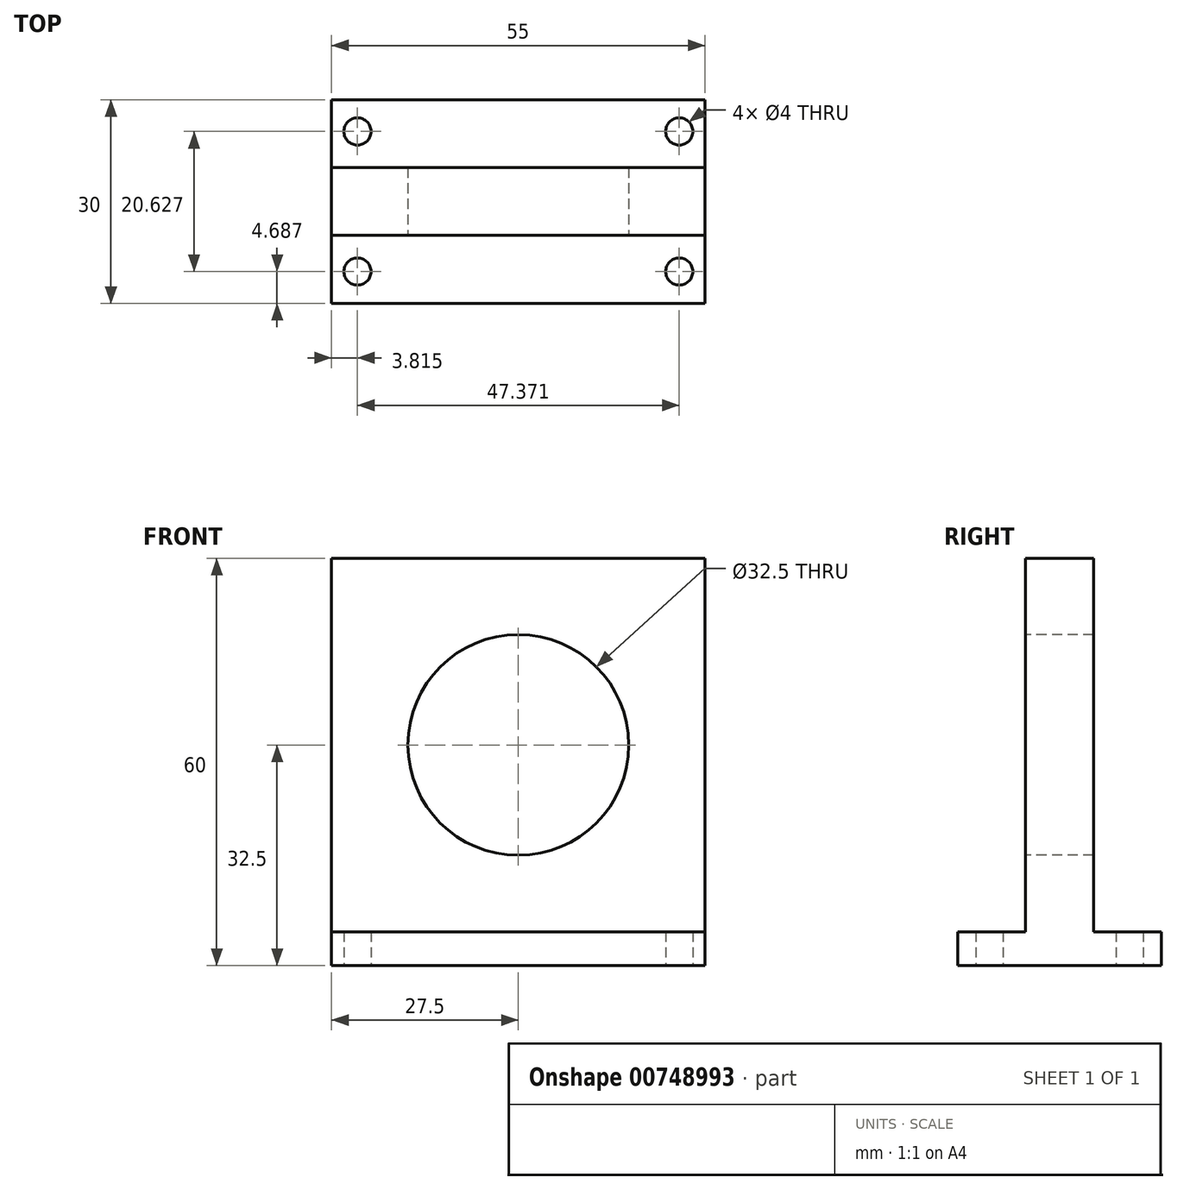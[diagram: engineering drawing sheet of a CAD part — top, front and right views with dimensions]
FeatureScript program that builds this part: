
annotation { "Feature Type Name" : "Feature", "Feature Type Description" : "" }
export const myFeature = defineFeature(function(context is Context, id is Id, definition is map)
    precondition{}
    {
        {
            var Q0;
            Q0=qCreatedBy(makeId("Top.planeOp"),FACE);
            var sketch = newSketch(context, id + "F0", { "sketchPlane" : qUnion([Q0])});
            skLineSegment(sketch, "E0.bottom", {"start": v(27.5, -5) * mm, "end": v(-27.5, -5) * mm});
            skLineSegment(sketch, "E0.top", {"start": v(27.5, 5) * mm, "end": v(-27.5, 5) * mm});
            skLineSegment(sketch, "E0.left", {"start": v(27.5, -5) * mm, "end": v(27.5, 5) * mm});
            skLineSegment(sketch, "E0.right", {"start": v(-27.5, -5) * mm, "end": v(-27.5, 5) * mm});
            skPoint(sketch, "E0.middle", {"position": v(0, 0) * mm});
            skSolve(sketch);
        }
        {
            var Q0;
            Q0 = qSketchRegion(id + "F0", true);
            extrude(context, id + "F1", {"entities" : qUnion([Q0]), "depth" : 55 * mm, "offsetDistance" : 25 * mm});
        }
        {
            var Q0;
            Q0=makeQuery(id+"F1.opExtrude","SWEPT_FACE",FACE,{"disambiguationData":[OSD([sQuery(id+"F0.wireOp",EDGE,"E0.bottom")])]});
            var sketch = newSketch(context, id + "F2", { "sketchPlane" : qUnion([Q0])});
            skCircle(sketch, "E1", {"center": v(0, 27.5) * mm, "radius": 16.25 * mm});
            skPoint(sketch, "E2.start.orphan", {"position": v(0, 55) * mm});
            skPoint(sketch, "E3.trimOffspring.end.orphan", {"position": v(-27.5, 27.5) * mm});
            skPoint(sketch, "E4.start.orphan", {"position": v(27.5, 27.5) * mm});
            skPoint(sketch, "E5.trimOffspring.end.orphan", {"position": v(0, 0) * mm});
            skSolve(sketch);
        }
        {
            var Q0;
            Q0 = qSketchRegion(id + "F2", true);
            extrude(context, id + "F3", {"entities" : qUnion([Q0]), "operationType" : NewBodyOperationType.REMOVE, "oppositeDirection" : true, "depth" : 25 * mm, "offsetDistance" : 25 * mm});
        }
        {
            var Q0;
            Q0=qCreatedBy(makeId("Top.planeOp"),FACE);
            var sketch = newSketch(context, id + "F4", { "sketchPlane" : qUnion([Q0])});
            skLineSegment(sketch, "E6.bottom", {"start": v(27.5, -15) * mm, "end": v(-27.5, -15) * mm});
            skLineSegment(sketch, "E6.top", {"start": v(27.5, 15) * mm, "end": v(-27.5, 15) * mm});
            skLineSegment(sketch, "E6.left", {"start": v(27.5, -15) * mm, "end": v(27.5, 15) * mm});
            skLineSegment(sketch, "E6.right", {"start": v(-27.5, -15) * mm, "end": v(-27.5, 15) * mm});
            skPoint(sketch, "E6.middle", {"position": v(0, 0) * mm});
            skSolve(sketch);
        }
        {
            var Q0;
            Q0=makeQuery(id+"F4.imprint","IMPRINT",FACE,{"disambiguationData":[TD([[makeQuery(id+"F4.imprint","IMPRINT",EDGE,{"derivedFrom":sQuery(id+"F4.wireOp",EDGE,"E6.bottom")}),-1.0]])]});
            extrude(context, id + "F5", {"entities" : qUnion([Q0]), "operationType" : NewBodyOperationType.ADD, "oppositeDirection" : true, "depth" : 5 * mm, "offsetDistance" : 25 * mm});
        }
        {
            var Q0;
            Q0=makeQuery(id+"F5.opExtrude","CAP_FACE",FACE,{"disambiguationData":[OSD([sQuery(id+"F4.wireOp",EDGE,"E6.bottom"),sQuery(id+"F4.wireOp",EDGE,"E6.top"),sQuery(id+"F4.wireOp",EDGE,"E6.left"),sQuery(id+"F4.wireOp",EDGE,"E6.right")])],"isStart":false});
            var sketch = newSketch(context, id + "F6", { "sketchPlane" : qUnion([Q0])});
            skCircle(sketch, "E7", {"center": v(23.69, 10.31) * mm, "radius": 2 * mm});
            skCircle(sketch, "E8.MirrorC", {"center": v(-23.69, 10.31) * mm, "radius": 2 * mm});
            skCircle(sketch, "E9.MirrorC", {"center": v(-23.69, -10.31) * mm, "radius": 2 * mm});
            skCircle(sketch, "E10.MirrorC", {"center": v(23.69, -10.31) * mm, "radius": 2 * mm});
            skSolve(sketch);
        }
        {
            var Q0;
            Q0 = qSketchRegion(id + "F6", true);
            extrude(context, id + "F7", {"entities" : qUnion([Q0]), "operationType" : NewBodyOperationType.REMOVE, "oppositeDirection" : true, "depth" : 25 * mm, "offsetDistance" : 25 * mm});
        }
    });
